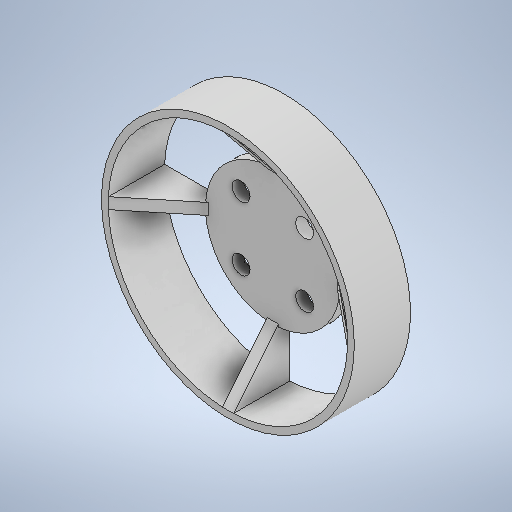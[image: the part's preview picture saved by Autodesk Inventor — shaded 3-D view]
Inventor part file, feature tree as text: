
AUTODESK INVENTOR PART (.ipt)
format: ipt  version: 2025.3 (Build 293356000, 356)  size: 324,608 bytes
history: native  units: mm
features: sketch x5, extrude x4, pattern_circular x2, other x1, hole x1
ambient origin geometry x8: Origin, YZ Plane, XZ Plane, XY Plane, X Axis, Y Axis, Z Axis, Center Point
bodies: Body1 (feature_tree)
feature tree (13):
  other  "ソリッド1"
  extrude  "ハブ"  Depth=2.0mm TaperAngle=0.0deg
  extrude  "リム"  Depth=10.0mm TaperAngle=0.0deg
  extrude  "スポーク"  Depth=11.5mm
  pattern_circular  "円形状パターン1"  [2 undecoded]
  hole  "フランジ取付穴"  [1 undecoded]
  extrude  "1層目をきれいに出力する溝"  Depth=16.0mm
  pattern_circular  "円形状パターン2"  Angle=45.0deg  [1 undecoded]
  sketch  "スケッチ1"
  sketch  "スケッチ2"
  sketch  "スケッチ5"
  sketch  "スケッチ6"
  sketch  "スケッチ8"
note: 4 required parameter values undecoded (feature->parameter linkage not recoverable at this tier; creation-order binding heuristic only, values carry confidence <= 0.55)
